FCSTD DOCUMENT  (FreeCAD 0.20R29410 (Git))
Label: DeltaPositions
License: All rights reserved
LicenseURL: http://en.wikipedia.org/wiki/All_rights_reserved
objects: Sketcher::SketchObject×1, PartDesign::Body×1
note: 2 computed .brp shape members not serialized (recipe doc carries the construction recipe); baked Part::Feature solids carry a one-line shape summary decoded from their .brp

FEATURE [Sketcher::SketchObject] Sketch
  FullyConstrained = true
  MapMode = 5
  Support = -> [XY_Plane]
  sketch-geometry (7):
    g0: Circle CenterX=0 CenterY=0 CenterZ=0 NormalX=0 NormalY=0 NormalZ=1 AngleXU=0 Radius=100
    g1: LineSegment StartX=0 StartY=0 StartZ=0 EndX=0 EndY=100 EndZ=0
    g2: LineSegment StartX=0 StartY=0 StartZ=0 EndX=-86.6025 EndY=-50 EndZ=0
    g3: LineSegment StartX=0 StartY=0 StartZ=0 EndX=86.6025 EndY=-50 EndZ=0
    g4: LineSegment StartX=0 StartY=100 StartZ=0 EndX=-86.6025 EndY=-50 EndZ=0
    g5: LineSegment StartX=-86.6025 StartY=-50 StartZ=0 EndX=86.6025 EndY=-50 EndZ=0
    g6: LineSegment StartX=0 StartY=100 StartZ=0 EndX=86.6025 EndY=-50 EndZ=0
  constraints (19):
    c: Coincident(g0,g-1)
    c: Radius(g0) = 100
    c: Coincident(g1,g0)
    c: PointOnObject(g1,g0)
    c: Vertical(g1)
    c: Coincident(g2,g0)
    c: PointOnObject(g2,g0)
    c: Coincident(g3,g0)
    c: PointOnObject(g3,g0)
    c: Coincident(g4,g1)
    c: Coincident(g4,g2)
    c: Coincident(g5,g2)
    c: Coincident(g5,g3)
    c: Coincident(g6,g1)
    c: Coincident(g6,g3)
    c: Equal(g5,g6)
    c: Equal(g6,g4)
    c: DistanceX(g3) = 86.6025
    c: DistanceY(g3) = -50
FEATURE [PartDesign::Body] Body
  Group = -> [Sketch]
  Origin = -> Origin
